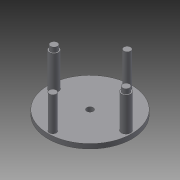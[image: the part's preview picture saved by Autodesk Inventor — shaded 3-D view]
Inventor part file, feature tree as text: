
AUTODESK INVENTOR PART (.ipt)
format: ipt  version: 2015 (Build 190159000, 159)  size: 117,248 bytes
history: native  units: mm
features: extrude x5, sketch x5, other x1
ambient origin geometry x8: Origin, YZ Plane, XZ Plane, XY Plane, X Axis, Y Axis, Z Axis, Center Point
bodies: Body1 (feature_tree)
feature tree (11):
  other  "ソリッド1"
  extrude  "押し出し1"  Depth=36.0mm
  extrude  "押し出し2"  Depth=2.0mm TaperAngle=0.0deg
  extrude  "押し出し3"  Depth=4.0mm
  extrude  "押し出し4"  Depth=4.0mm
  extrude  "押し出し5"  TaperAngle=0.0deg  [1 undecoded]
  sketch  "スケッチ1"
  sketch  "スケッチ2"
  sketch  "スケッチ3"
  sketch  "スケッチ4"
  sketch  "スケッチ5"
note: 1 required parameter value undecoded (feature->parameter linkage not recoverable at this tier; creation-order binding heuristic only, values carry confidence <= 0.55)
